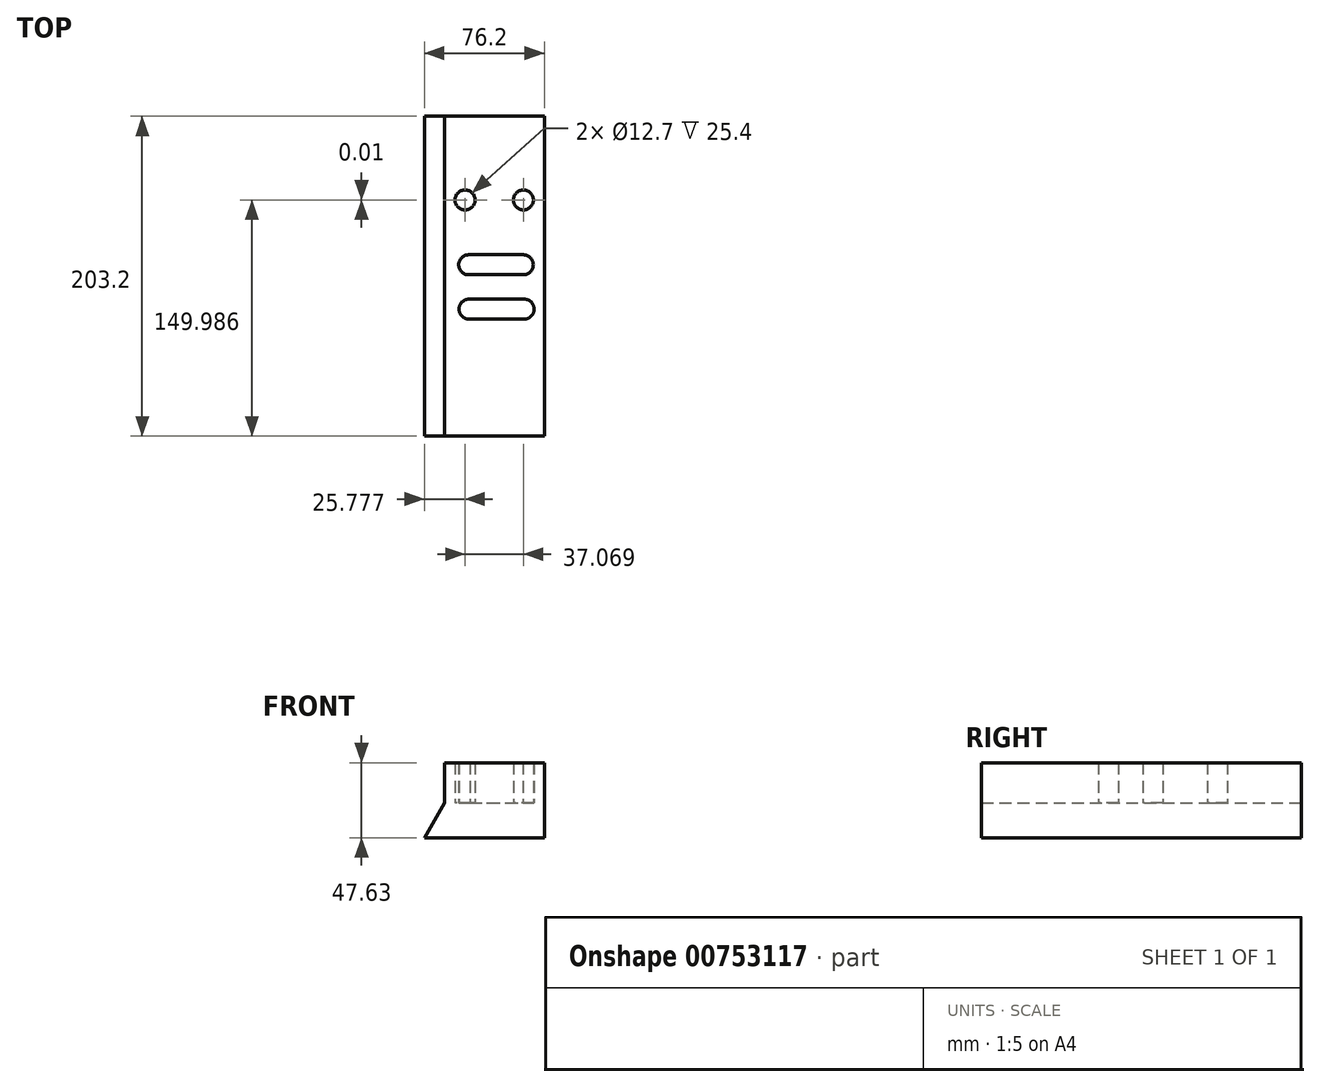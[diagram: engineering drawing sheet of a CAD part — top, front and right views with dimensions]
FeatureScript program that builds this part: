
annotation { "Feature Type Name" : "Feature", "Feature Type Description" : "" }
export const myFeature = defineFeature(function(context is Context, id is Id, definition is map)
    precondition{}
    {
        {
            var Q0;
            Q0=qCreatedBy(makeId("Front.planeOp"),FACE);
            var sketch = newSketch(context, id + "F0", { "sketchPlane" : qUnion([Q0])});
            skLineSegment(sketch, "E0", {"start": v(0, 0) * mm, "end": v(76.2, 0) * mm});
            skLineSegment(sketch, "E1", {"start": v(76.2, 0) * mm, "end": v(76.2, 22.23) * mm});
            skLineSegment(sketch, "E2", {"start": v(76.2, 22.23) * mm, "end": v(12.83, 22.23) * mm});
            skLineSegment(sketch, "E3", {"start": v(12.83, 22.23) * mm, "end": v(0, 0) * mm});
            skSolve(sketch);
        }
        {
            var Q0;
            Q0=makeQuery(id+"F0.imprint","IMPRINT",FACE,{"disambiguationData":[TD([[makeQuery(id+"F0.imprint","IMPRINT",EDGE,{"derivedFrom":sQuery(id+"F0.wireOp",EDGE,"E0")}),1.0]])]});
            extrude(context, id + "F1", {"entities" : qUnion([Q0]), "endBound" : BoundingType.SYMMETRIC, "depth" : 203.2 * mm, "offsetDistance" : 25.4 * mm});
        }
        {
            var Q0;
            Q0=makeQuery(id+"F1.opExtrude","SWEPT_FACE",FACE,{"disambiguationData":[OSD([sQuery(id+"F0.wireOp",EDGE,"E2")])]});
            var sketch = newSketch(context, id + "F2", { "sketchPlane" : qUnion([Q0])});
            skCircle(sketch, "E4", {"center": v(25.78, 48.4) * mm, "radius": 6.35 * mm});
            skCircle(sketch, "E5", {"center": v(62.85, 48.39) * mm, "radius": 6.35 * mm});
            skLineSegment(sketch, "E6", {"start": v(26.14, 54.74) * mm, "end": v(62.85, 54.74) * mm});
            skLineSegment(sketch, "E7", {"start": v(25.8, 42.05) * mm, "end": v(63.2, 42.05) * mm});
            skCircle(sketch, "E8", {"center": v(28.1, 7.2) * mm, "radius": 6.35 * mm});
            skCircle(sketch, "E9", {"center": v(62.77, 7.2) * mm, "radius": 6.35 * mm});
            skCircle(sketch, "E10", {"center": v(28.3, -20.98) * mm, "radius": 6.35 * mm});
            skCircle(sketch, "E11", {"center": v(63.33, -20.98) * mm, "radius": 6.35 * mm});
            skLineSegment(sketch, "E12", {"start": v(28.1, 13.55) * mm, "end": v(62.77, 13.55) * mm});
            skLineSegment(sketch, "E13", {"start": v(28.1, 0.85) * mm, "end": v(62.77, 0.85) * mm});
            skLineSegment(sketch, "E14", {"start": v(28.3, -14.63) * mm, "end": v(63.33, -14.63) * mm});
            skLineSegment(sketch, "E15", {"start": v(27.66, -27.3) * mm, "end": v(63.96, -27.3) * mm});
            skSolve(sketch);
        }
        {
            var Q0;
            {var subQ0=sQuery(id+"F2.wireOp",EDGE,"E6");Q0=makeQuery(id+"F2.imprint","IMPRINT",FACE,{"disambiguationData":[TD([[makeQuery(id+"F2.imprint","IMPRINT",EDGE,{"derivedFrom":subQ0}),-1.0]])]});}
            var sketch = newSketch(context, id + "F3", { "sketchPlane" : qUnion([Q0])});
            skSolve(sketch);
        }
        {
            var Q0;
            Q0 = qSketchRegion(id + "F3", true);
            var Q1;
            {var subQ0=sQuery(id+"F2.wireOp",EDGE,"E6");Q1=makeQuery(id+"F3.imprint","IMPRINT",FACE,{"disambiguationData":[TD([[makeQuery(id+"F3.imprint","IMPRINT",EDGE,{"derivedFrom":makeQuery(id+"F2.imprint","IMPRINT",EDGE,{"derivedFrom":subQ0})}),-1.0]])]});}
            var Q2;
            {var subQ14=sQuery(id+"F2.wireOp",EDGE,"E6");Q2=makeQuery(id+"F2.imprint","IMPRINT",FACE,{"disambiguationData":[TD([[makeQuery(id+"F2.imprint","IMPRINT",EDGE,{"derivedFrom":subQ14}),1.0]])]});}
            extrude(context, id + "F4", {"entities" : qUnion([Q0, Q1, Q2]), "operationType" : NewBodyOperationType.ADD, "depth" : 25.4 * mm, "offsetDistance" : 25.4 * mm});
        }
    });
